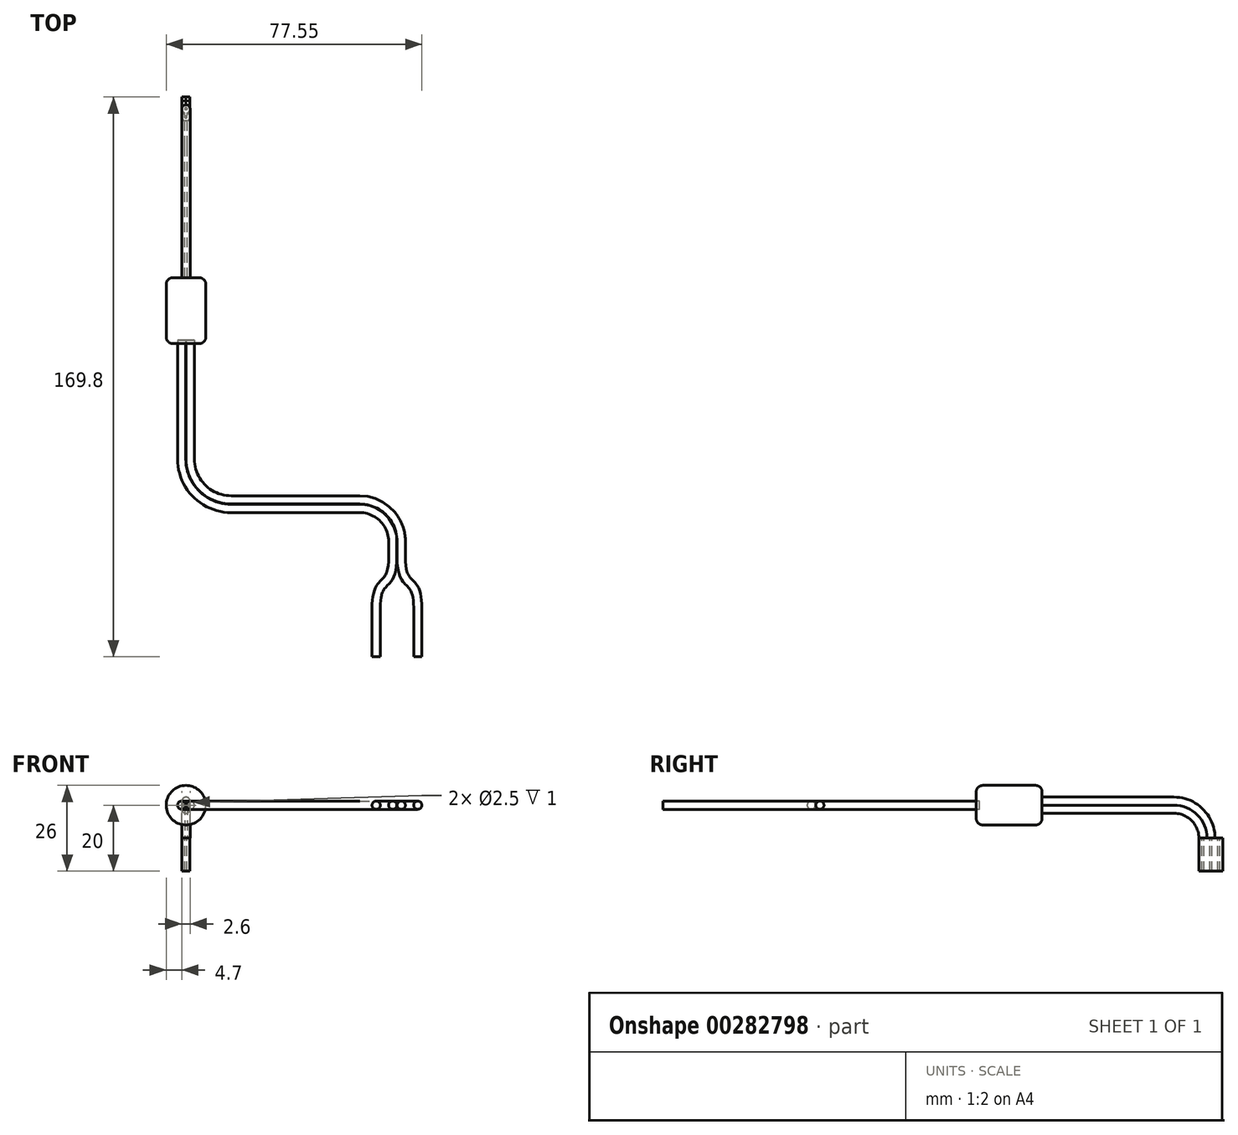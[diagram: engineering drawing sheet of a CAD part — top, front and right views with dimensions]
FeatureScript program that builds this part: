
annotation { "Feature Type Name" : "Feature", "Feature Type Description" : "" }
export const myFeature = defineFeature(function(context is Context, id is Id, definition is map)
    precondition{}
    {
        {
            var Q0;
            Q0=qCreatedBy(makeId("Top.planeOp"),FACE);
            var sketch = newSketch(context, id + "F0", { "sketchPlane" : qUnion([Q0])});
            skLineSegment(sketch, "E0.bottom", {"start": v(0, 0) * mm, "end": v(6, 0) * mm});
            skLineSegment(sketch, "E0.top", {"start": v(0, -20) * mm, "end": v(6, -20) * mm});
            skLineSegment(sketch, "E0.left", {"start": v(0, 0) * mm, "end": v(0, -20) * mm});
            skLineSegment(sketch, "E0.right", {"start": v(6, 0) * mm, "end": v(6, -20) * mm});
            skSolve(sketch);
        }
        {
            var Q0;
            Q0=qSketchRegion(id+"F0",true);
            var Q1;
            Q1=sQuery(id+"F0.wireOp",EDGE,"E0.left");
            revolve(context, id + "F1", {"entities" : qUnion([Q0]), "axis" : qUnion([Q1]), "revolveType" : RevolveType.FULL});
        }
        {
            var Q0;
            Q0=qCreatedBy(makeId("Right.planeOp"),FACE);
            var sketch = newSketch(context, id + "F2", { "sketchPlane" : qUnion([Q0])});
            skLineSegment(sketch, "E1", {"start": v(0, 0) * mm, "end": v(40, 0) * mm});
            skLineSegment(sketch, "E2", {"start": v(50, -10) * mm, "end": v(50, -10) * mm});
            skPoint(sketch, "E3.visualSharp", {"position": v(50, 0) * mm});
            skArc(sketch, "E3.filletArc", {"start": v(50, -10) * mm, "mid": v(47.07, -2.93) * mm, "end": v(40, 0) * mm});
            skSolve(sketch);
        }
        {
            var Q0;
            Q0=qCreatedBy(makeId("Front.planeOp"),FACE);
            var sketch = newSketch(context, id + "F3", { "sketchPlane" : qUnion([Q0])});
            skCircle(sketch, "E4", {"center": v(0, -1.2) * mm, "radius": 1.25 * mm});
            skCircle(sketch, "E5", {"center": v(0, 1.2) * mm, "radius": 1.25 * mm});
            skLineSegment(sketch, "E6", {"start": v(0, -1.2) * mm, "end": v(0, 0) * mm, "construction": true});
            skLineSegment(sketch, "E7", {"start": v(0, 1.2) * mm, "end": v(0, 0) * mm, "construction": true});
            skSolve(sketch);
        }
        {
            var Q0;
            Q0=qSketchRegion(id+"F3",true);
            var Q1;
            Q1=qConstructionFilter(qBodyType(qCreatedBy(id+"F2",EDGE),BodyType.WIRE),ConstructionObject.NO);
            sweep(context, id + "F4", {"operationType" : NewBodyOperationType.ADD, "profiles" : qUnion([Q0]), "path" : qUnion([Q1])});
        }
        {
            var Q0;
            Q0=makeQuery(id+"F4.opSweep","CAP_FACE",FACE,{"disambiguationData":[OSD([sQuery(id+"F2.wireOp",VERTEX,"E2.end"),sQuery(id+"F3.wireOp",EDGE,"E4"),sQuery(id+"F3.wireOp",EDGE,"E5")])],"isStart":false});
            var sketch = newSketch(context, id + "F5", { "sketchPlane" : qUnion([Q0])});
            skLineSegment(sketch, "E8.bottom", {"start": v(1.2, -52.4) * mm, "end": v(-1.2, -52.4) * mm});
            skLineSegment(sketch, "E8.top", {"start": v(1.2, -50) * mm, "end": v(-1.2, -50) * mm});
            skLineSegment(sketch, "E8.left", {"start": v(1.2, -52.4) * mm, "end": v(1.2, -50) * mm});
            skLineSegment(sketch, "E8.right", {"start": v(-1.2, -52.4) * mm, "end": v(-1.2, -50) * mm});
            skPoint(sketch, "E8.middle", {"position": v(0, -51.2) * mm});
            skLineSegment(sketch, "E9.top", {"start": v(1.2, -47.6) * mm, "end": v(-1.2, -47.6) * mm});
            skLineSegment(sketch, "E9.left", {"start": v(1.2, -50) * mm, "end": v(1.2, -47.6) * mm});
            skLineSegment(sketch, "E9.right", {"start": v(-1.2, -50) * mm, "end": v(-1.2, -47.6) * mm});
            skPoint(sketch, "E9.middle", {"position": v(0, -48.8) * mm});
            skLineSegment(sketch, "E10.bottom", {"start": v(0.3, -51.5) * mm, "end": v(-0.3, -51.5) * mm});
            skLineSegment(sketch, "E10.top", {"start": v(0.3, -50.9) * mm, "end": v(-0.3, -50.9) * mm});
            skLineSegment(sketch, "E10.left", {"start": v(0.3, -51.5) * mm, "end": v(0.3, -50.9) * mm});
            skLineSegment(sketch, "E10.right", {"start": v(-0.3, -51.5) * mm, "end": v(-0.3, -50.9) * mm});
            skLineSegment(sketch, "E11.bottom", {"start": v(-0.3, -48.5) * mm, "end": v(0.3, -48.5) * mm});
            skLineSegment(sketch, "E11.top", {"start": v(-0.3, -49.1) * mm, "end": v(0.3, -49.1) * mm});
            skLineSegment(sketch, "E11.left", {"start": v(-0.3, -48.5) * mm, "end": v(-0.3, -49.1) * mm});
            skLineSegment(sketch, "E11.right", {"start": v(0.3, -48.5) * mm, "end": v(0.3, -49.1) * mm});
            skLineSegment(sketch, "E12.top", {"start": v(1.2, -54.8) * mm, "end": v(-1.2, -54.8) * mm});
            skLineSegment(sketch, "E12.left", {"start": v(1.2, -52.4) * mm, "end": v(1.2, -54.8) * mm});
            skLineSegment(sketch, "E12.right", {"start": v(-1.2, -52.4) * mm, "end": v(-1.2, -54.8) * mm});
            skLineSegment(sketch, "E13.bottom", {"start": v(-0.3, -53.3) * mm, "end": v(0.3, -53.3) * mm});
            skLineSegment(sketch, "E13.top", {"start": v(-0.3, -53.9) * mm, "end": v(0.3, -53.9) * mm});
            skLineSegment(sketch, "E13.left", {"start": v(-0.3, -53.3) * mm, "end": v(-0.3, -53.9) * mm});
            skLineSegment(sketch, "E13.right", {"start": v(0.3, -53.3) * mm, "end": v(0.3, -53.9) * mm});
            skPoint(sketch, "E13.middle", {"position": v(0, -53.6) * mm});
            skLineSegment(sketch, "E14", {"start": v(0, -53.6) * mm, "end": v(0, -51.2) * mm, "construction": true});
            skSolve(sketch);
        }
        {
            var Q0;
            Q0=qSketchRegion(id+"F5",true);
            extrude(context, id + "F6", {"entities" : qUnion([Q0]), "operationType" : NewBodyOperationType.ADD, "depth" : 10 * mm});
        }
        {
            var Q0;
            Q0=makeQuery(id+"F1.opRevolve","SWEPT_FACE",FACE,{"disambiguationData":[OSD([sQuery(id+"F0.wireOp",EDGE,"E0.top")])]});
            var sketch = newSketch(context, id + "F7", { "sketchPlane" : qUnion([Q0])});
            skCircle(sketch, "E15", {"center": v(1.3, 0) * mm, "radius": 1.25 * mm});
            skCircle(sketch, "E16", {"center": v(-1.3, 0) * mm, "radius": 1.25 * mm});
            skLineSegment(sketch, "E17", {"start": v(-1.3, 0) * mm, "end": v(0, 0) * mm, "construction": true});
            skLineSegment(sketch, "E18", {"start": v(0, 0) * mm, "end": v(1.3, 0) * mm, "construction": true});
            skSolve(sketch);
        }
        {
            var Q0;
            Q0=makeQuery(id+"F1.opRevolve","SWEPT_EDGE",EDGE,{"disambiguationData":[OSD([sQuery(id+"F0.wireOp",EDGE,"E0.bottom"),sQuery(id+"F0.wireOp",EDGE,"E0.right")])]});
            var Q1;
            Q1=makeQuery(id+"F1.opRevolve","SWEPT_EDGE",EDGE,{"disambiguationData":[OSD([sQuery(id+"F0.wireOp",EDGE,"E0.top"),sQuery(id+"F0.wireOp",EDGE,"E0.right")])]});
            fillet(context, id + "F8", {"entities" : qUnion([Q0, Q1]), "radius" : 2 * mm, "tangentPropagation" : true, "allowEdgeOverflow" : false});
        }
        {
            var Q0;
            Q0=makeQuery(id+"F7.imprint","IMPRINT",FACE,{"disambiguationData":[TD([[makeQuery(id+"F7.imprint","IMPRINT",EDGE,{"derivedFrom":sQuery(id+"F7.wireOp",EDGE,"E15")}),1.0]])]});
            var Q1;
            Q1=makeQuery(id+"F7.imprint","IMPRINT",FACE,{"disambiguationData":[TD([[makeQuery(id+"F7.imprint","IMPRINT",EDGE,{"derivedFrom":sQuery(id+"F7.wireOp",EDGE,"E16")}),1.0]])]});
            extrude(context, id + "F9", {"entities" : qUnion([Q0, Q1]), "operationType" : NewBodyOperationType.REMOVE, "oppositeDirection" : true, "depth" : 1 * mm});
        }
        {
            var Q0;
            Q0=qCreatedBy(makeId("Top.planeOp"),FACE);
            var sketch = newSketch(context, id + "F10", { "sketchPlane" : qUnion([Q0])});
            skLineSegment(sketch, "E19", {"start": v(-1.3, -20) * mm, "end": v(-1.3, -55) * mm});
            skLineSegment(sketch, "E20", {"start": v(13.7, -70) * mm, "end": v(52.7, -70) * mm});
            skLineSegment(sketch, "E21", {"start": v(62.7, -80) * mm, "end": v(62.7, -85) * mm});
            skPoint(sketch, "E22.visualSharp", {"position": v(-1.3, -70) * mm});
            skArc(sketch, "E22.filletArc", {"start": v(-1.3, -55) * mm, "mid": v(3.1, -65.6) * mm, "end": v(13.7, -70) * mm});
            skPoint(sketch, "E23.visualSharp", {"position": v(62.7, -70) * mm});
            skArc(sketch, "E23.filletArc", {"start": v(62.7, -80) * mm, "mid": v(59.77, -72.93) * mm, "end": v(52.7, -70) * mm});
            skLineSegment(sketch, "E24.1", {"start": v(1.3, -20) * mm, "end": v(1.3, -55) * mm});
            skArc(sketch, "E24.2", {"start": v(1.3, -55) * mm, "mid": v(4.93, -63.77) * mm, "end": v(13.7, -67.4) * mm});
            skLineSegment(sketch, "E24.3", {"start": v(13.7, -67.4) * mm, "end": v(52.7, -67.4) * mm});
            skArc(sketch, "E24.4", {"start": v(65.3, -80) * mm, "mid": v(61.6, -71.1) * mm, "end": v(52.7, -67.4) * mm});
            skLineSegment(sketch, "E25", {"start": v(62.7, -80) * mm, "end": v(65.3, -80) * mm, "construction": true});
            skLineSegment(sketch, "E26", {"start": v(64, -78.2) * mm, "end": v(64, -80) * mm, "construction": true});
            skFitSpline(sketch, "E27", {"points": [v(62.7, -85) * mm, v(60.2, -92.5) * mm, v(57.7, -100) * mm], "startDerivative": vector(0, -30) * mm, "endDerivative": vector(0, -30) * mm});
            skLineSegment(sketch, "E28", {"start": v(62.7, -90) * mm, "end": v(62.7, -85) * mm, "construction": true});
            skLineSegment(sketch, "E29", {"start": v(57.7, -95) * mm, "end": v(57.7, -100) * mm, "construction": true});
            skLineSegment(sketch, "E30", {"start": v(57.7, -100) * mm, "end": v(62.7, -85) * mm, "construction": true});
            skLineSegment(sketch, "E31.MirrorCS", {"start": v(65.3, -80) * mm, "end": v(65.3, -85) * mm});
            skFitSpline(sketch, "E32.MirrorCS", {"points": [v(65.3, -85) * mm, v(67.8, -92.5) * mm, v(70.3, -100) * mm], "startDerivative": vector(0, -30) * mm, "endDerivative": vector(0, -30) * mm});
            skLineSegment(sketch, "E33", {"start": v(57.7, -100) * mm, "end": v(57.7, -115) * mm});
            skLineSegment(sketch, "E34.MirrorCS", {"start": v(70.3, -100) * mm, "end": v(70.3, -115) * mm});
            skSolve(sketch);
        }
        {
            var Q0;
            Q0=makeQuery(id+"F7.imprint","IMPRINT",FACE,{"disambiguationData":[TD([[makeQuery(id+"F7.imprint","IMPRINT",EDGE,{"derivedFrom":sQuery(id+"F7.wireOp",EDGE,"E15")}),1.0]])]});
            var Q1;
            Q1=sQuery(id+"F10.wireOp",EDGE,"E24.1");
            var Q2;
            Q2=sQuery(id+"F10.wireOp",EDGE,"E24.2");
            var Q3;
            Q3=sQuery(id+"F10.wireOp",EDGE,"E24.3");
            var Q4;
            Q4=sQuery(id+"F10.wireOp",EDGE,"E24.4");
            var Q5;
            Q5=sQuery(id+"F10.wireOp",EDGE,"E31.MirrorCS");
            var Q6;
            Q6=sQuery(id+"F10.wireOp",EDGE,"E32.MirrorCS");
            var Q7;
            Q7=sQuery(id+"F10.wireOp",EDGE,"E34.MirrorCS");
            sweep(context, id + "F11", {"profiles" : qUnion([Q0]), "path" : qUnion([Q1, Q2, Q3, Q4, Q5, Q6, Q7])});
        }
        {
            var Q0;
            Q0=makeQuery(id+"F7.imprint","IMPRINT",FACE,{"disambiguationData":[TD([[makeQuery(id+"F7.imprint","IMPRINT",EDGE,{"derivedFrom":sQuery(id+"F7.wireOp",EDGE,"E16")}),1.0]])]});
            var Q1;
            Q1=sQuery(id+"F10.wireOp",EDGE,"E19");
            var Q2;
            Q2=sQuery(id+"F10.wireOp",EDGE,"E22.filletArc");
            var Q3;
            Q3=sQuery(id+"F10.wireOp",EDGE,"E20");
            var Q4;
            Q4=sQuery(id+"F10.wireOp",EDGE,"E23.filletArc");
            var Q5;
            Q5=sQuery(id+"F10.wireOp",EDGE,"E21");
            var Q6;
            Q6=sQuery(id+"F10.wireOp",EDGE,"E27");
            var Q7;
            Q7=sQuery(id+"F10.wireOp",EDGE,"E33");
            sweep(context, id + "F12", {"profiles" : qUnion([Q0]), "path" : qUnion([Q1, Q2, Q3, Q4, Q5, Q6, Q7])});
        }
    });
